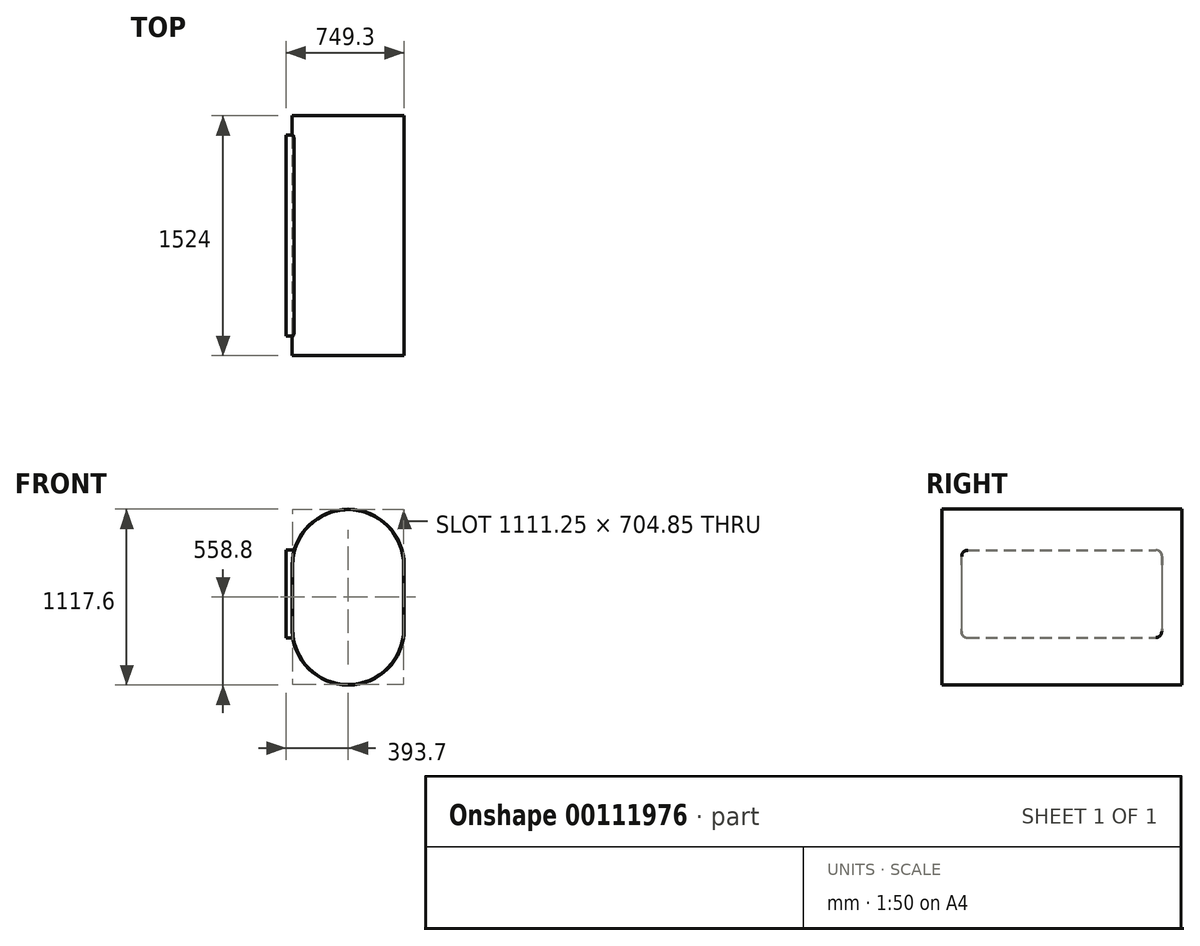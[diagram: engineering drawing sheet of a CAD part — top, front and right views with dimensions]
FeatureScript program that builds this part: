
annotation { "Feature Type Name" : "Feature", "Feature Type Description" : "" }
export const myFeature = defineFeature(function(context is Context, id is Id, definition is map)
    precondition{}
    {
        {
            var Q0;
            Q0=qCreatedBy(makeId("Front.planeOp"),FACE);
            var sketch = newSketch(context, id + "F0", { "sketchPlane" : qUnion([Q0])});
            skLineSegment(sketch, "E0", {"start": v(-355.6, 203.2) * mm, "end": v(-355.6, -203.2) * mm});
            skPoint(sketch, "E1", {"position": v(-355.6, 0) * mm});
            skLineSegment(sketch, "E2.MirrorCS", {"start": v(355.6, 203.2) * mm, "end": v(355.6, -203.2) * mm});
            skArc(sketch, "E3", {"start": v(355.6, 203.2) * mm, "mid": v(0, 558.8) * mm, "end": v(-355.6, 203.2) * mm});
            skArc(sketch, "E4.MirrorCS", {"start": v(355.6, -203.2) * mm, "mid": v(0, -558.8) * mm, "end": v(-355.6, -203.2) * mm});
            skArc(sketch, "E5.0", {"start": v(352.42, 203.2) * mm, "mid": v(0, 555.63) * mm, "end": v(-352.43, 203.2) * mm});
            skLineSegment(sketch, "E5.1", {"start": v(352.43, 203.2) * mm, "end": v(352.43, -203.2) * mm});
            skArc(sketch, "E5.2", {"start": v(352.43, -203.2) * mm, "mid": v(0, -555.63) * mm, "end": v(-352.43, -203.2) * mm});
            skLineSegment(sketch, "E5.3", {"start": v(-352.43, 203.2) * mm, "end": v(-352.43, -203.2) * mm});
            skLineSegment(sketch, "E6", {"start": v(457.2, -203.2) * mm, "end": v(-457.2, -203.2) * mm, "construction": true});
            skSolve(sketch);
        }
        {
            var Q0;
            Q0 = qSketchRegion(id + "F0", true);
            extrude(context, id + "F1", {"entities" : qUnion([Q0]), "depth" : 1524 * mm, "symmetric" : true});
        }
        {
            var Q0;
            Q0=makeQuery(id+"F1.opExtrude","SWEPT_FACE",FACE,{"disambiguationData":[OSD([sQuery(id+"F0.wireOp",EDGE,"E0")])]});
            var sketch = newSketch(context, id + "F2", { "sketchPlane" : qUnion([Q0])});
            skLineSegment(sketch, "E7.bottom", {"start": v(-596.9, 298.16) * mm, "end": v(596.9, 298.16) * mm});
            skLineSegment(sketch, "E7.top", {"start": v(-596.9, -257.25) * mm, "end": v(596.9, -257.25) * mm});
            skLineSegment(sketch, "E7.left", {"start": v(-635, 260.06) * mm, "end": v(-635, -219.15) * mm});
            skLineSegment(sketch, "E7.right", {"start": v(635, 260.06) * mm, "end": v(635, -219.15) * mm});
            skPoint(sketch, "E8", {"position": v(0, 298.16) * mm});
            skPoint(sketch, "E9", {"position": v(0, 203.2) * mm});
            skPoint(sketch, "E10.visualSharp", {"position": v(-635, 298.16) * mm});
            skArc(sketch, "E10.filletArc", {"start": v(-596.9, 298.16) * mm, "mid": v(-623.84, 287) * mm, "end": v(-635, 260.06) * mm});
            skPoint(sketch, "E11.visualSharp", {"position": v(635, 298.16) * mm});
            skArc(sketch, "E11.filletArc", {"start": v(635, 260.06) * mm, "mid": v(623.84, 287) * mm, "end": v(596.9, 298.16) * mm});
            skPoint(sketch, "E12.visualSharp", {"position": v(635, -257.25) * mm});
            skArc(sketch, "E12.filletArc", {"start": v(596.9, -257.25) * mm, "mid": v(623.84, -246.09) * mm, "end": v(635, -219.15) * mm});
            skPoint(sketch, "E13.visualSharp", {"position": v(-635, -257.25) * mm});
            skArc(sketch, "E13.filletArc", {"start": v(-635, -219.15) * mm, "mid": v(-623.84, -246.09) * mm, "end": v(-596.9, -257.25) * mm});
            skSolve(sketch);
        }
        {
            var Q0;
            Q0 = qSketchRegion(id + "F2", true);
            extrude(context, id + "F3", {"entities" : qUnion([Q0]), "operationType" : NewBodyOperationType.REMOVE, "oppositeDirection" : true, "depth" : 25.4 * mm});
        }
        {
            var Q0;
            {var subQ2=sQuery(id+"F0.wireOp",EDGE,"E0");Q0=makeQuery(id+"F3.boolean.opBoolean","SPLIT",FACE,{"disambiguationData":[TD([makeQuery(id+"F3.opExtrude","SWEPT_FACE",FACE,{"disambiguationData":[OSD([sQuery(id+"F2.wireOp",EDGE,"E7.left")])]})])],"derivedFrom":makeQuery(id+"F1.opExtrude","SWEPT_FACE",FACE,{"disambiguationData":[OSD([subQ2])]})});}
            cPlane(context, id + "F4", {"entities" : qUnion([Q0]), "cplaneType" : CPlaneType.OFFSET, "offset" : 38.1 * mm, "width" : 152.4 * mm, "height" : 152.4 * mm});
        }
        {
            var Q0;
            Q0=qCreatedBy(id+"F4.planeOp",FACE);
            var sketch = newSketch(context, id + "F5", { "sketchPlane" : qUnion([Q0])});
            skLineSegment(sketch, "E14.0", {"start": v(-596.9, -257.25) * mm, "end": v(596.9, -257.25) * mm});
            skArc(sketch, "E14.1", {"start": v(-635, -219.15) * mm, "mid": v(-623.84, -246.09) * mm, "end": v(-596.9, -257.25) * mm});
            skLineSegment(sketch, "E14.2", {"start": v(-635, -203.2) * mm, "end": v(-635, -219.15) * mm});
            skLineSegment(sketch, "E14.3", {"start": v(-635, 203.2) * mm, "end": v(-635, -203.2) * mm});
            skLineSegment(sketch, "E14.4", {"start": v(-635, 203.2) * mm, "end": v(-635, 260.06) * mm});
            skArc(sketch, "E14.5", {"start": v(-596.9, 298.16) * mm, "mid": v(-623.84, 287) * mm, "end": v(-635, 260.06) * mm});
            skLineSegment(sketch, "E14.6", {"start": v(596.9, 298.16) * mm, "end": v(-596.9, 298.16) * mm});
            skArc(sketch, "E14.7", {"start": v(596.9, -257.25) * mm, "mid": v(623.84, -246.09) * mm, "end": v(635, -219.15) * mm});
            skLineSegment(sketch, "E14.8", {"start": v(635, -203.2) * mm, "end": v(635, -219.15) * mm});
            skLineSegment(sketch, "E14.9", {"start": v(635, 203.2) * mm, "end": v(635, -203.2) * mm});
            skLineSegment(sketch, "E14.10", {"start": v(635, 203.2) * mm, "end": v(635, 260.06) * mm});
            skArc(sketch, "E14.11", {"start": v(635, 260.06) * mm, "mid": v(623.84, 287) * mm, "end": v(596.9, 298.16) * mm});
            skArc(sketch, "E15.0", {"start": v(638.17, 260.06) * mm, "mid": v(626.09, 289.25) * mm, "end": v(596.9, 301.34) * mm});
            skLineSegment(sketch, "E15.1", {"start": v(-638.18, -203.2) * mm, "end": v(-638.18, -219.15) * mm});
            skLineSegment(sketch, "E15.2", {"start": v(-638.18, 203.2) * mm, "end": v(-638.18, -203.2) * mm});
            skLineSegment(sketch, "E15.3", {"start": v(-638.18, 203.2) * mm, "end": v(-638.18, 260.06) * mm});
            skArc(sketch, "E15.4", {"start": v(-596.9, 301.34) * mm, "mid": v(-626.09, 289.25) * mm, "end": v(-638.17, 260.06) * mm});
            skArc(sketch, "E15.5", {"start": v(-638.17, -219.15) * mm, "mid": v(-626.09, -248.33) * mm, "end": v(-596.9, -260.42) * mm});
            skLineSegment(sketch, "E15.6", {"start": v(596.9, 301.34) * mm, "end": v(-596.9, 301.34) * mm});
            skLineSegment(sketch, "E15.7", {"start": v(-596.9, -260.42) * mm, "end": v(596.9, -260.42) * mm});
            skArc(sketch, "E15.8", {"start": v(596.9, -260.42) * mm, "mid": v(626.09, -248.33) * mm, "end": v(638.18, -219.15) * mm});
            skLineSegment(sketch, "E15.9", {"start": v(638.17, -203.2) * mm, "end": v(638.17, -219.15) * mm});
            skLineSegment(sketch, "E15.10", {"start": v(638.17, 203.2) * mm, "end": v(638.17, -203.2) * mm});
            skLineSegment(sketch, "E15.11", {"start": v(638.18, 203.2) * mm, "end": v(638.18, 260.06) * mm});
            skSolve(sketch);
        }
        {
            var Q0;
            Q0 = qSketchRegion(id + "F5", true);
            extrude(context, id + "F6", {"entities" : qUnion([Q0]), "endBound" : BoundingType.UP_TO_NEXT, "oppositeDirection" : true, "depth" : 25.4 * mm});
        }
        {
            var Q0;
            Q0=makeQuery(id+"F1.opExtrude","CAP_FACE",FACE,{"disambiguationData":[OSD([sQuery(id+"F0.wireOp",EDGE,"E0"),sQuery(id+"F0.wireOp",EDGE,"E2.MirrorCS"),sQuery(id+"F0.wireOp",EDGE,"E3"),sQuery(id+"F0.wireOp",EDGE,"E4.MirrorCS"),sQuery(id+"F0.wireOp",EDGE,"E5.0"),sQuery(id+"F0.wireOp",EDGE,"E5.1"),sQuery(id+"F0.wireOp",EDGE,"E5.2"),sQuery(id+"F0.wireOp",EDGE,"E5.3")])],"isStart":true});
            var sketch = newSketch(context, id + "F7", { "sketchPlane" : qUnion([Q0])});
            skSolve(sketch);
        }
        {
            var Q0;
            Q0=makeQuery(id+"F7.imprint","IMPRINT",FACE,{"disambiguationData":[TD([[makeQuery(id+"F7.imprint","IMPRINT",EDGE,{"derivedFrom":makeQuery(id+"F1.opExtrude","CAP_EDGE",EDGE,{"disambiguationData":[OSD([sQuery(id+"F0.wireOp",EDGE,"E5.0")])],"isStart":true})}),-1.0]])]});
            extrude(context, id + "F8", {"entities" : qUnion([Q0]), "oppositeDirection" : true, "depth" : 3.17 * mm});
        }
    });
